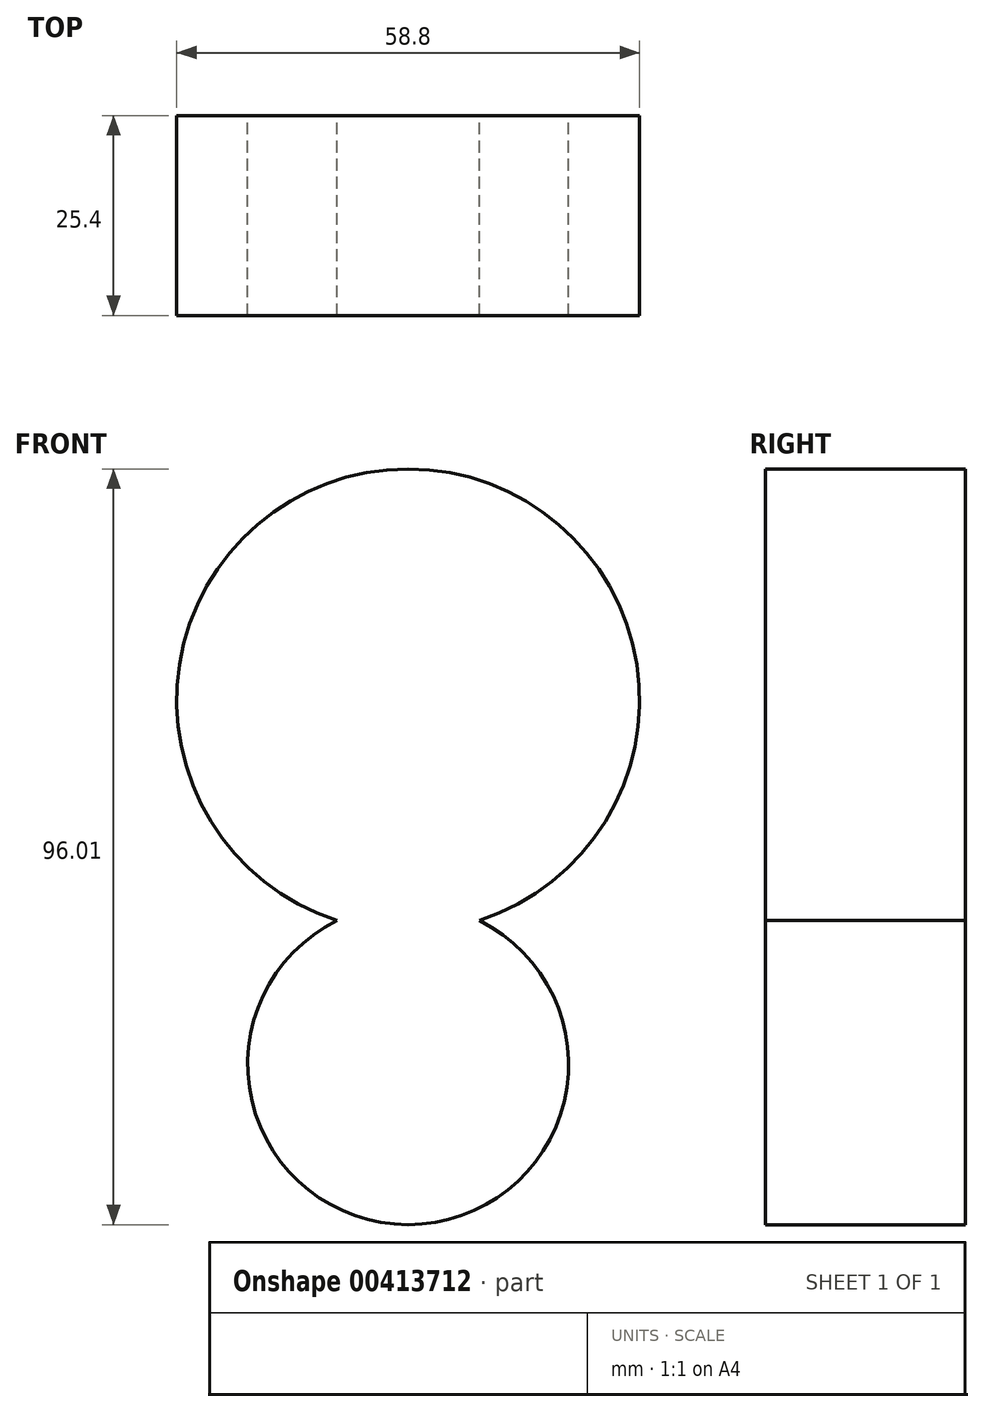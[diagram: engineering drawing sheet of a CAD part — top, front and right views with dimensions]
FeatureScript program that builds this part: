
annotation { "Feature Type Name" : "Feature", "Feature Type Description" : "" }
export const myFeature = defineFeature(function(context is Context, id is Id, definition is map)
    precondition{}
    {
        {
            var Q0;
            Q0=qCreatedBy(makeId("Front.planeOp"),FACE);
            var sketch = newSketch(context, id + "F0", { "sketchPlane" : qUnion([Q0])});
            skCircle(sketch, "E0", {"center": v(0, 0) * mm, "radius": 20.38 * mm});
            skSolve(sketch);
        }
        {
            var Q0;
            Q0 = qSketchRegion(id + "F0", true);
            extrude(context, id + "F1", {"entities" : qUnion([Q0]), "depth" : 25.4 * mm});
        }
        {
            var Q0;
            Q0=qCreatedBy(makeId("Front.planeOp"),FACE);
            var sketch = newSketch(context, id + "F2", { "sketchPlane" : qUnion([Q0])});
            skCircle(sketch, "E1", {"center": v(0, 46.23) * mm, "radius": 29.4 * mm});
            skSolve(sketch);
        }
        {
            var Q0;
            Q0 = qSketchRegion(id + "F2", true);
            extrude(context, id + "F3", {"entities" : qUnion([Q0]), "operationType" : NewBodyOperationType.ADD, "depth" : 25.4 * mm});
        }
        {
            var Q0;
            Q0=qCreatedBy(makeId("Front.planeOp"),FACE);
            var sketch = newSketch(context, id + "F4", { "sketchPlane" : qUnion([Q0])});
            skLineSegment(sketch, "E2", {"start": v(-219.82, 0) * mm, "end": v(-219.82, -38.5) * mm});
            skLineSegment(sketch, "E3", {"start": v(-219.82, -38.5) * mm, "end": v(-184, -38.5) * mm});
            skSolve(sketch);
        }
        {
            var Q0;
            Q0=qCreatedBy(makeId("Front.planeOp"),FACE);
            var sketch = newSketch(context, id + "F5", { "sketchPlane" : qUnion([Q0])});
            skLineSegment(sketch, "E4", {"start": v(-185.5, 0) * mm, "end": v(0, 0) * mm});
            skLineSegment(sketch, "E5", {"start": v(0, 0) * mm, "end": v(-185.5, 0) * mm});
            skLineSegment(sketch, "E6", {"start": v(-185.5, -35.53) * mm, "end": v(-185.5, 0) * mm});
            skLineSegment(sketch, "E7", {"start": v(-218.5, 0) * mm, "end": v(-185.5, 0) * mm});
            skSolve(sketch);
        }
        {
            var Q0;
            Q0=sQuery(id+"F5.wireOp",EDGE,"E6");
            var Q1;
            Q1=sQuery(id+"F4.wireOp",EDGE,"E3");
            var Q2;
            Q2=sQuery(id+"F4.wireOp",EDGE,"E2");
            var Q3;
            Q3=sQuery(id+"F5.wireOp",EDGE,"E7");
            extrude(context, id + "F6", {"bodyType" : ToolBodyType.SURFACE, "surfaceEntities" : qUnion([Q0, Q1, Q2, Q3]), "depth" : 115.12 * mm});
        }
        {
            var Q0;
            Q0=qCreatedBy(makeId("Front.planeOp"),FACE);
            var sketch = newSketch(context, id + "F7", { "sketchPlane" : qUnion([Q0])});
            skLineSegment(sketch, "E8", {"start": v(0, 0) * mm, "end": v(-186.4, 0) * mm});
            skSolve(sketch);
        }
        {
            var Q0;
            Q0 = qSketchRegion(id + "F7", true);
            var Q1;
            Q1=sQuery(id+"F7.wireOp",EDGE,"E8");
            extrude(context, id + "F8", {"entities" : qUnion([Q0]), "bodyType" : ToolBodyType.SURFACE, "surfaceEntities" : qUnion([Q1]), "depth" : 37 * mm});
        }
    });
